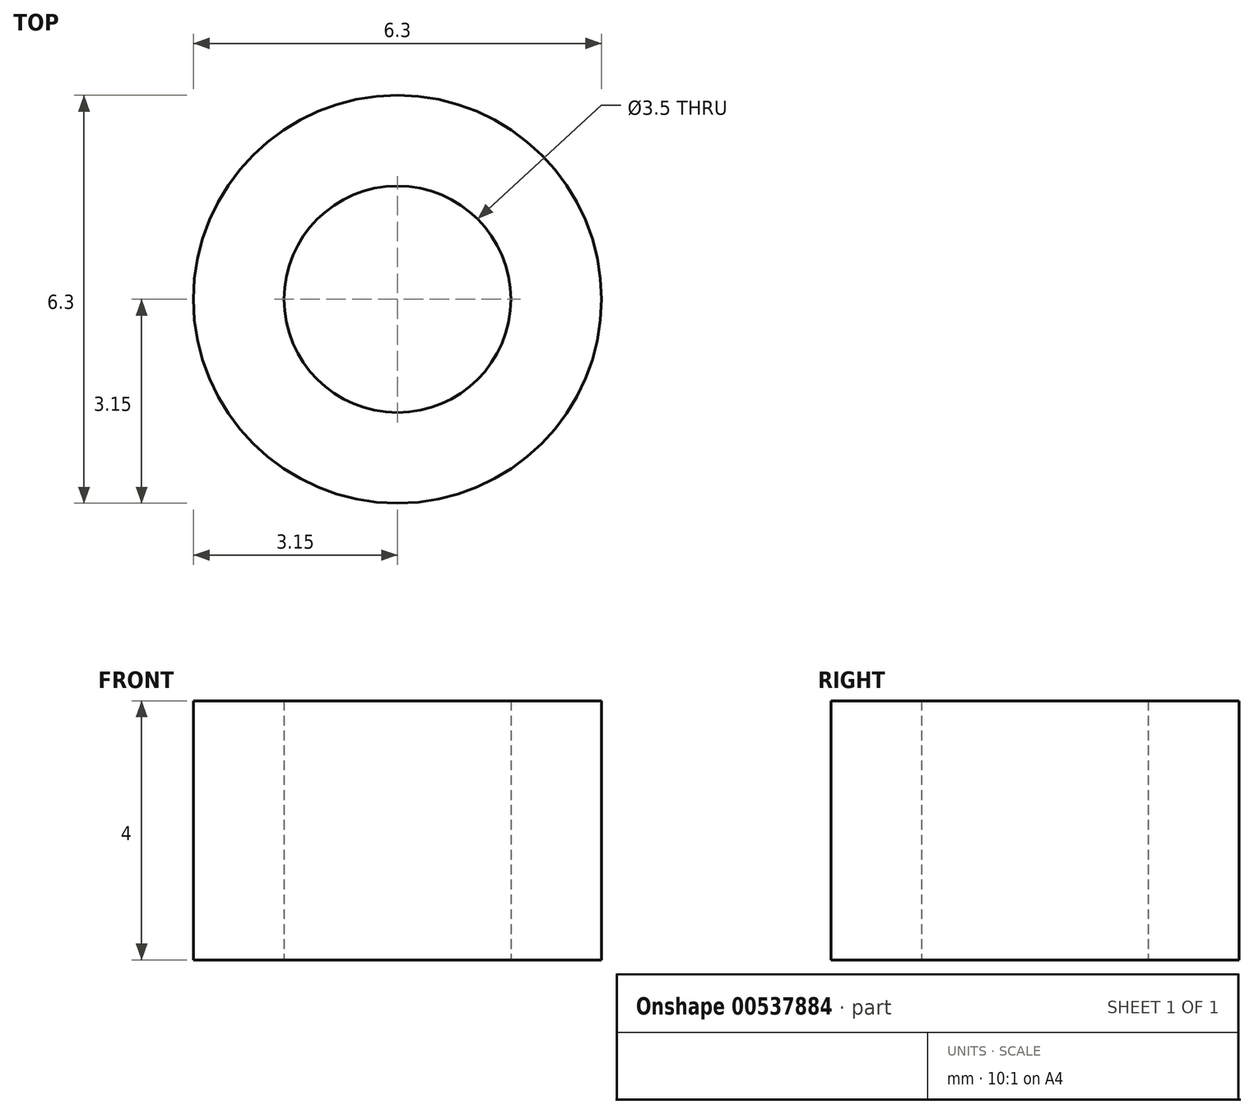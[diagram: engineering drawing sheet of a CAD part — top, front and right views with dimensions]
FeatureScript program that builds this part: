
annotation { "Feature Type Name" : "Feature", "Feature Type Description" : "" }
export const myFeature = defineFeature(function(context is Context, id is Id, definition is map)
    precondition{}
    {
        {
            var Q0;
            Q0=qCreatedBy(makeId("Top.planeOp"),FACE);
            var sketch = newSketch(context, id + "F0", { "sketchPlane" : qUnion([Q0])});
            skCircle(sketch, "E0", {"center": v(0, 0) * mm, "radius": 3.15 * mm});
            skCircle(sketch, "E1", {"center": v(0, 0) * mm, "radius": 1.75 * mm});
            skSolve(sketch);
        }
        {
            var Q0;
            Q0=makeQuery(id+"F0.imprint","IMPRINT",FACE,{"disambiguationData":[TD([[makeQuery(id+"F0.imprint","IMPRINT",EDGE,{"derivedFrom":sQuery(id+"F0.wireOp",EDGE,"E0")}),1.0]])]});
            extrude(context, id + "F1", {"entities" : qUnion([Q0]), "depth" : 4 * mm, "offsetDistance" : 25 * mm});
        }
    });
